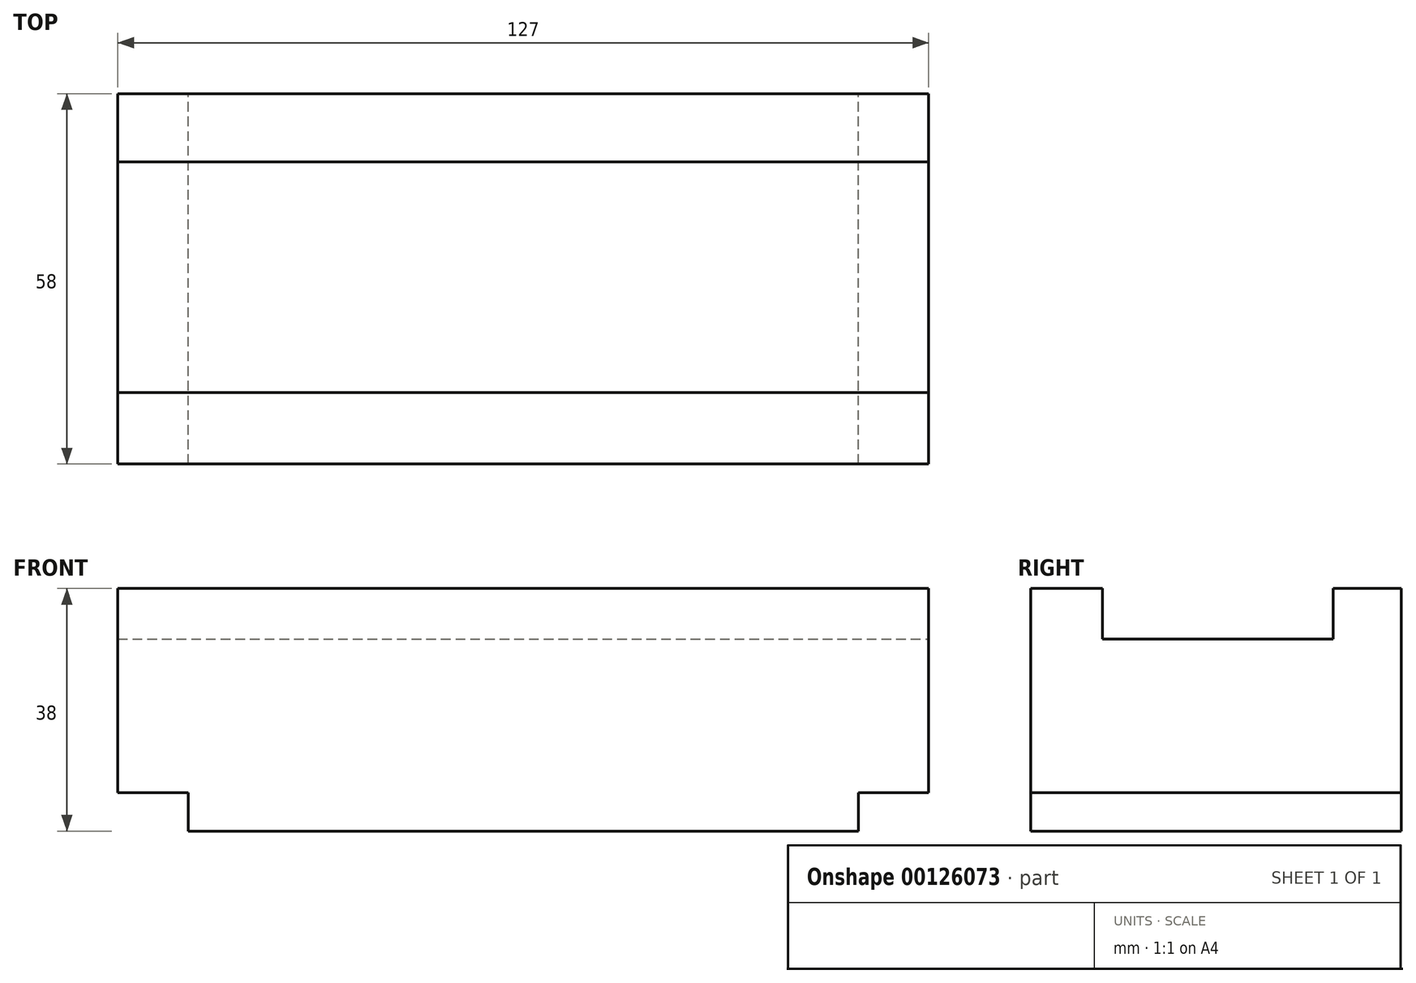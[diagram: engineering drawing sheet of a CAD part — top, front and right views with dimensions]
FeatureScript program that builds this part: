
annotation { "Feature Type Name" : "Feature", "Feature Type Description" : "" }
export const myFeature = defineFeature(function(context is Context, id is Id, definition is map)
    precondition{}
    {
        {
            var Q0;
            Q0=qCreatedBy(makeId("Front.planeOp"),FACE);
            var sketch = newSketch(context, id + "F0", { "sketchPlane" : qUnion([Q0])});
            skLineSegment(sketch, "E0.bottom", {"start": v(0, 0) * mm, "end": v(127, 0) * mm});
            skLineSegment(sketch, "E0.top", {"start": v(0, 38) * mm, "end": v(127, 38) * mm});
            skLineSegment(sketch, "E0.left", {"start": v(0, 0) * mm, "end": v(0, 38) * mm});
            skLineSegment(sketch, "E0.right", {"start": v(127, 0) * mm, "end": v(127, 38) * mm});
            skSolve(sketch);
        }
        {
            var Q0;
            Q0 = qSketchRegion(id + "F0", true);
            extrude(context, id + "F1", {"entities" : qUnion([Q0]), "depth" : 58 * mm});
        }
        {
            var Q0;
            Q0=makeQuery(id+"F1.opExtrude","SWEPT_FACE",FACE,{"disambiguationData":[OSD([sQuery(id+"F0.wireOp",EDGE,"E0.right")])]});
            var sketch = newSketch(context, id + "F2", { "sketchPlane" : qUnion([Q0])});
            skLineSegment(sketch, "E1.bottom", {"start": v(-58, 0) * mm, "end": v(0, 0) * mm});
            skLineSegment(sketch, "E1.top", {"start": v(-58, 6) * mm, "end": v(0, 6) * mm});
            skLineSegment(sketch, "E1.left", {"start": v(-58, 0) * mm, "end": v(-58, 6) * mm});
            skLineSegment(sketch, "E1.right", {"start": v(0, 0) * mm, "end": v(0, 6) * mm});
            skSolve(sketch);
        }
        {
            var Q0;
            Q0 = qSketchRegion(id + "F2", true);
            extrude(context, id + "F3", {"entities" : qUnion([Q0]), "operationType" : NewBodyOperationType.REMOVE, "oppositeDirection" : true, "depth" : 11 * mm});
        }
        {
            var Q0;
            Q0=makeQuery(id+"F1.opExtrude","SWEPT_FACE",FACE,{"disambiguationData":[OSD([sQuery(id+"F0.wireOp",EDGE,"E0.left")])]});
            var sketch = newSketch(context, id + "F4", { "sketchPlane" : qUnion([Q0])});
            skLineSegment(sketch, "E2.bottom", {"start": v(0, 0) * mm, "end": v(58, 0) * mm});
            skLineSegment(sketch, "E2.top", {"start": v(0, 6) * mm, "end": v(58, 6) * mm});
            skLineSegment(sketch, "E2.left", {"start": v(0, 0) * mm, "end": v(0, 6) * mm});
            skLineSegment(sketch, "E2.right", {"start": v(58, 0) * mm, "end": v(58, 6) * mm});
            skSolve(sketch);
        }
        {
            var Q0;
            Q0 = qSketchRegion(id + "F4", true);
            extrude(context, id + "F5", {"entities" : qUnion([Q0]), "operationType" : NewBodyOperationType.REMOVE, "oppositeDirection" : true, "depth" : 11 * mm});
        }
        {
            var Q0;
            Q0=makeQuery(id+"F1.opExtrude","SWEPT_FACE",FACE,{"disambiguationData":[OSD([sQuery(id+"F0.wireOp",EDGE,"E0.right")])]});
            var sketch = newSketch(context, id + "F6", { "sketchPlane" : qUnion([Q0])});
            skLineSegment(sketch, "E3.bottom", {"start": v(-46.8, 38) * mm, "end": v(-10.66, 38) * mm});
            skLineSegment(sketch, "E3.top", {"start": v(-46.8, 30.06) * mm, "end": v(-10.66, 30.06) * mm});
            skLineSegment(sketch, "E3.left", {"start": v(-46.8, 38) * mm, "end": v(-46.8, 30.06) * mm});
            skLineSegment(sketch, "E3.right", {"start": v(-10.66, 38) * mm, "end": v(-10.66, 30.06) * mm});
            skSolve(sketch);
        }
        {
            var Q0;
            Q0 = qSketchRegion(id + "F6", true);
            extrude(context, id + "F7", {"entities" : qUnion([Q0]), "operationType" : NewBodyOperationType.REMOVE, "oppositeDirection" : true, "depth" : 200 * mm});
        }
    });
